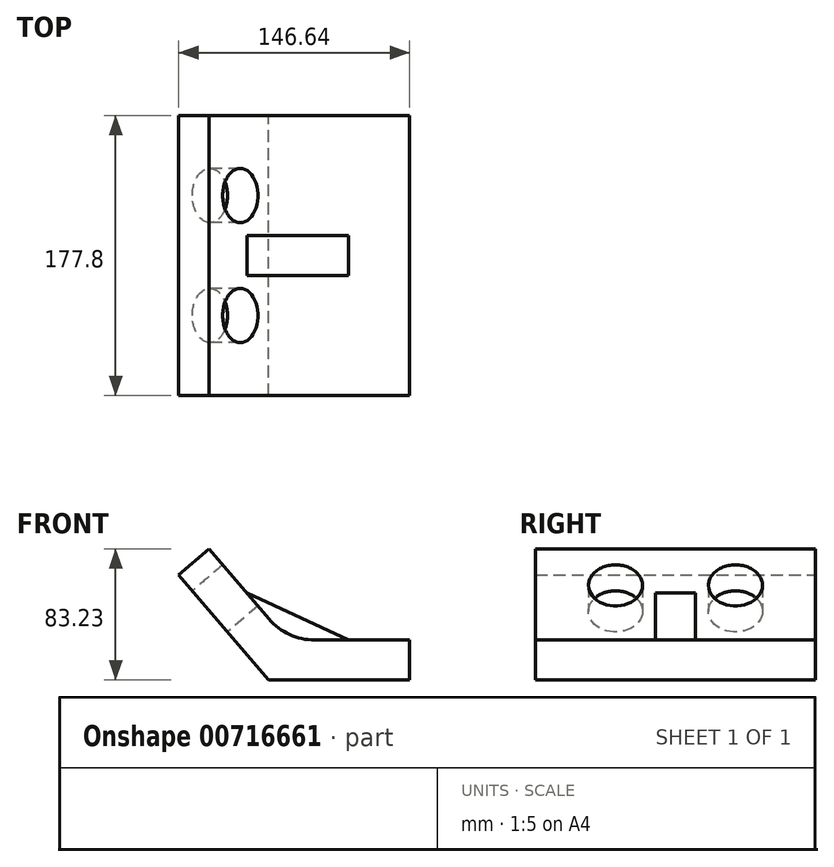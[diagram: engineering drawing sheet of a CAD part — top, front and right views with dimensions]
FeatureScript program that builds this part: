
annotation { "Feature Type Name" : "Feature", "Feature Type Description" : "" }
export const myFeature = defineFeature(function(context is Context, id is Id, definition is map)
    precondition{}
    {
        {
            var Q0;
            Q0=qCreatedBy(makeId("Front.planeOp"),FACE);
            var sketch = newSketch(context, id + "F0", { "sketchPlane" : qUnion([Q0])});
            skLineSegment(sketch, "E0", {"start": v(0, 0) * mm, "end": v(89.58, 0) * mm});
            skLineSegment(sketch, "E1", {"start": v(89.58, 0) * mm, "end": v(89.58, 25.4) * mm});
            skLineSegment(sketch, "E2", {"start": v(89.58, 25.4) * mm, "end": v(29.25, 25.4) * mm});
            skLineSegment(sketch, "E3", {"start": v(0.3, 38.74) * mm, "end": v(-37.75, 83.23) * mm});
            skLineSegment(sketch, "E4", {"start": v(-37.75, 83.23) * mm, "end": v(-57.06, 66.73) * mm});
            skLineSegment(sketch, "E5", {"start": v(-57.06, 66.73) * mm, "end": v(0, 0) * mm});
            skPoint(sketch, "E6.visualSharp", {"position": v(11.7, 25.4) * mm});
            skArc(sketch, "E6.filletArc", {"start": v(0.3, 38.74) * mm, "mid": v(13.31, 28.9) * mm, "end": v(29.25, 25.4) * mm});
            skSolve(sketch);
        }
        {
            var Q0;
            Q0=qSketchRegion(id+"F0",true);
            extrude(context, id + "F1", {"entities" : qUnion([Q0]), "endBound" : BoundingType.SYMMETRIC, "depth" : 177.8 * mm, "offsetDistance" : 25.4 * mm});
        }
        {
            var Q0;
            Q0=qCreatedBy(makeId("Front.planeOp"),FACE);
            var sketch = newSketch(context, id + "F2", { "sketchPlane" : qUnion([Q0])});
            skLineSegment(sketch, "E7", {"start": v(-33.02, 77.7) * mm, "end": v(11.7, 25.4) * mm});
            skLineSegment(sketch, "E8", {"start": v(11.7, 25.4) * mm, "end": v(81.48, 25.4) * mm});
            skLineSegment(sketch, "E9", {"start": v(11.7, 25.4) * mm, "end": v(-13.75, 55.17) * mm});
            skLineSegment(sketch, "E10", {"start": v(-13.75, 55.17) * mm, "end": v(50.87, 25.4) * mm});
            skLineSegment(sketch, "E11", {"start": v(50.87, 25.4) * mm, "end": v(11.7, 25.4) * mm});
            skSolve(sketch);
        }
        {
            var Q0;
            Q0=qSketchRegion(id+"F2",true);
            extrude(context, id + "F3", {"entities" : qUnion([Q0]), "operationType" : NewBodyOperationType.ADD, "endBound" : BoundingType.SYMMETRIC, "depth" : 25.4 * mm});
        }
        {
            var Q0;
            Q0=makeQuery(id+"F1.opExtrude","SWEPT_FACE",FACE,{"disambiguationData":[OSD([sQuery(id+"F0.wireOp",EDGE,"E5")])]});
            var sketch = newSketch(context, id + "F4", { "sketchPlane" : qUnion([Q0])});
            skCircle(sketch, "E12", {"center": v(-38.1, 57.32) * mm, "radius": 17.18 * mm});
            skCircle(sketch, "E13", {"center": v(38.1, 57.32) * mm, "radius": 17.18 * mm});
            skSolve(sketch);
        }
        {
            var Q0;
            Q0=qSketchRegion(id+"F4",true);
            extrude(context, id + "F5", {"entities" : qUnion([Q0]), "operationType" : NewBodyOperationType.REMOVE, "endBound" : BoundingType.THROUGH_ALL, "oppositeDirection" : true, "depth" : 25.4 * mm});
        }
    });
